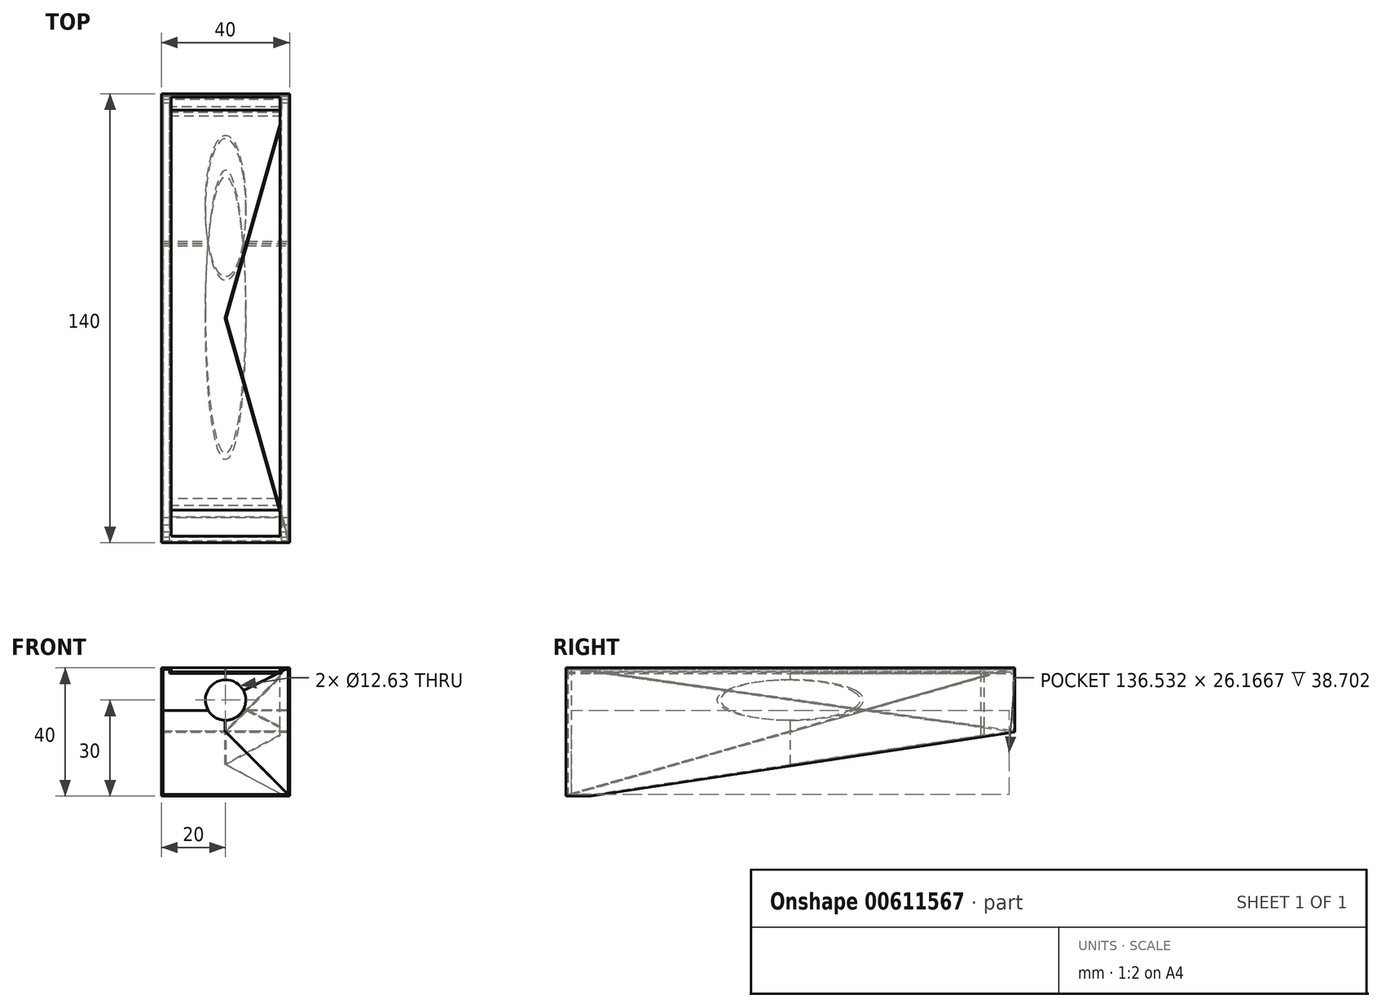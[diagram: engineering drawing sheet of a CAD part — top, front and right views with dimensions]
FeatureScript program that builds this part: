
annotation { "Feature Type Name" : "Feature", "Feature Type Description" : "" }
export const myFeature = defineFeature(function(context is Context, id is Id, definition is map)
    precondition{}
    {
        {
            var Q0;
            Q0=qCreatedBy(makeId("Front.planeOp"),FACE);
            var sketch = newSketch(context, id + "F0", { "sketchPlane" : qUnion([Q0])});
            skLineSegment(sketch, "E0.bottom", {"start": v(-15, 20) * mm, "end": v(15, 20) * mm});
            skLineSegment(sketch, "E0.top", {"start": v(-15, -20) * mm, "end": v(15, -20) * mm});
            skLineSegment(sketch, "E0.left", {"start": v(-20, 15) * mm, "end": v(-20, -15) * mm});
            skLineSegment(sketch, "E0.right", {"start": v(20, 15) * mm, "end": v(20, -15) * mm});
            skPoint(sketch, "E0.middle", {"position": v(0, 0) * mm});
            skPoint(sketch, "E1.visualSharp", {"position": v(-20, -20) * mm});
            skPoint(sketch, "E2.visualSharp", {"position": v(20, -20) * mm});
            skLineSegment(sketch, "E3", {"start": v(-20, -15) * mm, "end": v(20, -15) * mm});
            skLineSegment(sketch, "E4", {"start": v(-20, -15) * mm, "end": v(-20, -11.86) * mm});
            skLineSegment(sketch, "E5", {"start": v(-20, -15) * mm, "end": v(-17, -15) * mm});
            skLineSegment(sketch, "E6", {"start": v(-17, -15) * mm, "end": v(-17, 20) * mm});
            skLineSegment(sketch, "E7", {"start": v(-17, 20) * mm, "end": v(-17, 15) * mm});
            skLineSegment(sketch, "E8", {"start": v(-17, 15) * mm, "end": v(-20, 15) * mm});
            skLineSegment(sketch, "E9.MirrorCS", {"start": v(17, -15) * mm, "end": v(17, 20) * mm});
            skLineSegment(sketch, "E10.MirrorCS", {"start": v(20, 20) * mm, "end": v(20, -15) * mm});
            skLineSegment(sketch, "E11.MirrorCS", {"start": v(17, 15) * mm, "end": v(20, 15) * mm});
            skLineSegment(sketch, "E12", {"start": v(-18.5, 15) * mm, "end": v(-18.5, -15) * mm});
            skLineSegment(sketch, "E13", {"start": v(-18.5, -5.26) * mm, "end": v(-18.5, -3.26) * mm});
            skLineSegment(sketch, "E14", {"start": v(-18.5, 2.74) * mm, "end": v(-18.5, 4.74) * mm});
            skLineSegment(sketch, "E15", {"start": v(-15, -20) * mm, "end": v(-15, -15) * mm});
            skLineSegment(sketch, "E16", {"start": v(-15, -17.5) * mm, "end": v(15, -17.5) * mm});
            skLineSegment(sketch, "E17", {"start": v(15, -17.5) * mm, "end": v(15, -20) * mm});
            skLineSegment(sketch, "E18", {"start": v(15, -17.5) * mm, "end": v(15, -15) * mm});
            skLineSegment(sketch, "E19", {"start": v(-15, -15) * mm, "end": v(-18.54, -18.54) * mm});
            skLineSegment(sketch, "E20", {"start": v(-18.54, -18.54) * mm, "end": v(-16.77, -16.77) * mm});
            skLineSegment(sketch, "E21", {"start": v(-20, -15) * mm, "end": v(-15, -20) * mm});
            skCircle(sketch, "E22", {"center": v(0, -17.5) * mm, "radius": 2.07 * mm});
            skCircle(sketch, "E23", {"center": v(-10.25, -17.5) * mm, "radius": 1.14 * mm});
            skCircle(sketch, "E24", {"center": v(-5.95, -17.5) * mm, "radius": 1.97 * mm});
            skCircle(sketch, "E25.MirrorC", {"center": v(5.95, -17.5) * mm, "radius": 1.97 * mm});
            skCircle(sketch, "E26.MirrorC", {"center": v(10.25, -17.5) * mm, "radius": 1.14 * mm});
            skLineSegment(sketch, "E27", {"start": v(-17, 20) * mm, "end": v(17, 20) * mm});
            skPoint(sketch, "E28.visualSharp", {"position": v(-20, 20) * mm});
            skPoint(sketch, "E29.visualSharp", {"position": v(20, 20) * mm});
            skLineSegment(sketch, "E30", {"start": v(-17, 17.5) * mm, "end": v(17, 17.5) * mm});
            skLineSegment(sketch, "E31", {"start": v(-17, 18.83) * mm, "end": v(17, 18.83) * mm});
            skLineSegment(sketch, "E32", {"start": v(-20, 15) * mm, "end": v(-20, 20) * mm});
            skLineSegment(sketch, "E33", {"start": v(17, 20) * mm, "end": v(20, 20) * mm});
            skLineSegment(sketch, "E34", {"start": v(-20, 20) * mm, "end": v(-17, 20) * mm});
            skLineSegment(sketch, "E35", {"start": v(15, -20) * mm, "end": v(20, -20) * mm});
            skLineSegment(sketch, "E36", {"start": v(20, -15) * mm, "end": v(20, -20) * mm});
            skLineSegment(sketch, "E37", {"start": v(-15, -20) * mm, "end": v(-20, -20) * mm});
            skLineSegment(sketch, "E38", {"start": v(-20, -15) * mm, "end": v(-20, -20) * mm});
            skSolve(sketch);
        }
        {
            var Q0;
            {var subQ5=sQuery(id+"F0.wireOp",EDGE,"E11.MirrorCS");Q0=makeQuery(id+"F0.imprint","IMPRINT",FACE,{"disambiguationData":[TD([[makeQuery(id+"F0.imprint","IMPRINT",EDGE,{"derivedFrom":subQ5}),1.0]])]});}
            var Q1;
            {var subQ0=sQuery(id+"F0.wireOp",EDGE,"E21");var subQ3=sQuery(id+"F0.wireOp",EDGE,"kyP0Ghf2-8tRf-b2os-GJ9Y-R51s7YL5zU5A");var subQ5=makeQuery(id+"F0.imprint","INTERSECT",VERTEX,{"disambiguationData":[OD(0.0)],"derivedFrom":[subQ0,subQ3]});Q1=makeQuery(id+"F0.imprint","IMPRINT",FACE,{"disambiguationData":[TD([[makeQuery(id+"F0.imprint","IMPRINT",EDGE,{"disambiguationData":[TD([[subQ5,-1.0]])],"derivedFrom":subQ3}),-1.0]])]});}
            var Q2;
            {var subQ0=sQuery(id+"F0.wireOp",EDGE,"E21");var subQ3=sQuery(id+"F0.wireOp",EDGE,"kyP0Ghf2-8tRf-b2os-GJ9Y-R51s7YL5zU5A");var subQ5=makeQuery(id+"F0.imprint","INTERSECT",VERTEX,{"disambiguationData":[OD(1.0)],"derivedFrom":[subQ0,subQ3]});Q2=makeQuery(id+"F0.imprint","IMPRINT",FACE,{"disambiguationData":[TD([[makeQuery(id+"F0.imprint","IMPRINT",EDGE,{"disambiguationData":[TD([[subQ5,1.0]])],"derivedFrom":subQ3}),-1.0]])]});}
            var Q3;
            {var subQ1=sQuery(id+"F0.wireOp",EDGE,"E2.filletArc");var subQ3=sQuery(id+"F0.wireOp",EDGE,"8bdb658c-147e-4b0e-9f76-7d081b696ae10.MirrorC");var subQ4=makeQuery(id+"F0.imprint","INTERSECT",VERTEX,{"derivedFrom":[subQ1,subQ3]});Q3=makeQuery(id+"F0.imprint","IMPRINT",FACE,{"disambiguationData":[TD([[makeQuery(id+"F0.imprint","IMPRINT",EDGE,{"disambiguationData":[TD([[subQ4,-1.0]])],"derivedFrom":subQ3}),1.0]])]});}
            var Q4;
            {var subQ1=sQuery(id+"F0.wireOp",EDGE,"E2.filletArc");var subQ3=sQuery(id+"F0.wireOp",EDGE,"8bdb658c-147e-4b0e-9f76-7d081b696ae10.MirrorC");var subQ4=makeQuery(id+"F0.imprint","INTERSECT",VERTEX,{"derivedFrom":[subQ1,subQ3]});Q4=makeQuery(id+"F0.imprint","IMPRINT",FACE,{"disambiguationData":[TD([[makeQuery(id+"F0.imprint","IMPRINT",EDGE,{"disambiguationData":[TD([[subQ4,1.0]])],"derivedFrom":subQ3}),1.0]])]});}
            var Q5;
            {var subQ0=sQuery(id+"F0.wireOp",EDGE,"E7");Q5=makeQuery(id+"F0.imprint","IMPRINT",FACE,{"disambiguationData":[TD([[makeQuery(id+"F0.imprint","IMPRINT",EDGE,{"derivedFrom":subQ0}),-1.0]])]});}
            var Q6;
            {var subQ0=sQuery(id+"F0.wireOp",EDGE,"E8");var subQ1=sQuery(id+"F0.wireOp",EDGE,"E0.left");var subQ2=makeQuery(id+"F0.imprint","INTERSECT",VERTEX,{"derivedFrom":[subQ1,subQ0]});Q6=makeQuery(id+"F0.imprint","IMPRINT",FACE,{"disambiguationData":[TD([[makeQuery(id+"F0.imprint","IMPRINT",EDGE,{"disambiguationData":[TD([[subQ2,-1.0]])],"derivedFrom":subQ1}),1.0]])]});}
            var Q7;
            {var subQ0=sQuery(id+"F0.wireOp",EDGE,"1121410c-8889-4fde-b7d4-53cf977519030.MirrorC");var subQ1=sQuery(id+"F0.wireOp",EDGE,"E0.left");var subQ2=makeQuery(id+"F0.imprint","INTERSECT",VERTEX,{"derivedFrom":[subQ1,subQ0]});Q7=makeQuery(id+"F0.imprint","IMPRINT",FACE,{"disambiguationData":[TD([[makeQuery(id+"F0.imprint","IMPRINT",EDGE,{"disambiguationData":[TD([[subQ2,-1.0]])],"derivedFrom":subQ1}),1.0]])]});}
            var Q8;
            {var subQ1=sQuery(id+"F0.wireOp",EDGE,"E0.left");var subQ5=sQuery(id+"F0.wireOp",EDGE,"3be5d0f7-e66a-4034-bf2c-b5a2b3a159480.MirrorC");var subQ6=makeQuery(id+"F0.imprint","INTERSECT",VERTEX,{"derivedFrom":[subQ1,subQ5]});Q8=makeQuery(id+"F0.imprint","IMPRINT",FACE,{"disambiguationData":[TD([[makeQuery(id+"F0.imprint","IMPRINT",EDGE,{"disambiguationData":[TD([[subQ6,-1.0]])],"derivedFrom":subQ1}),1.0]])]});}
            var Q9;
            {var subQ0=sQuery(id+"F0.wireOp",EDGE,"fb5a3924-ac59-4bed-af84-7003ddc445cf0.MirrorC");var subQ1=sQuery(id+"F0.wireOp",EDGE,"E0.left");var subQ2=makeQuery(id+"F0.imprint","INTERSECT",VERTEX,{"derivedFrom":[subQ1,subQ0]});Q9=makeQuery(id+"F0.imprint","IMPRINT",FACE,{"disambiguationData":[TD([[makeQuery(id+"F0.imprint","IMPRINT",EDGE,{"disambiguationData":[TD([[subQ2,-1.0]])],"derivedFrom":subQ1}),1.0]])]});}
            var Q10;
            {var subQ1=sQuery(id+"F0.wireOp",EDGE,"E0.left");var subQ7=sQuery(id+"F0.wireOp",EDGE,"804b6b5c-8591-4f70-8d60-dec1e7231a500.MirrorC");var subQ9=makeQuery(id+"F0.imprint","INTERSECT",VERTEX,{"derivedFrom":[subQ1,subQ7]});Q10=makeQuery(id+"F0.imprint","IMPRINT",FACE,{"disambiguationData":[TD([[makeQuery(id+"F0.imprint","IMPRINT",EDGE,{"disambiguationData":[TD([[subQ9,-1.0]])],"derivedFrom":subQ1}),1.0]])]});}
            var Q11;
            {var subQ0=sQuery(id+"F0.wireOp",EDGE,"UupdKjqE-uhdA-a4V7-ZC8J-dwgjoSrKTdi6");var subQ1=sQuery(id+"F0.wireOp",EDGE,"E0.left");var subQ2=makeQuery(id+"F0.imprint","INTERSECT",VERTEX,{"derivedFrom":[subQ1,subQ0]});Q11=makeQuery(id+"F0.imprint","IMPRINT",FACE,{"disambiguationData":[TD([[makeQuery(id+"F0.imprint","IMPRINT",EDGE,{"disambiguationData":[TD([[subQ2,-1.0]])],"derivedFrom":subQ1}),1.0]])]});}
            var Q12;
            {var subQ1=sQuery(id+"F0.wireOp",EDGE,"E5");var subQ3=sQuery(id+"F0.wireOp",EDGE,"kyP0Ghf2-8tRf-b2os-GJ9Y-R51s7YL5zU5A");var subQ4=makeQuery(id+"F0.imprint","INTERSECT",VERTEX,{"derivedFrom":[subQ1,subQ3]});Q12=makeQuery(id+"F0.imprint","IMPRINT",FACE,{"disambiguationData":[TD([[makeQuery(id+"F0.imprint","IMPRINT",EDGE,{"disambiguationData":[TD([[subQ4,-1.0]])],"derivedFrom":subQ3}),-1.0]])]});}
            var Q13;
            {var subQ0=sQuery(id+"F0.wireOp",EDGE,"819de83c-ce93-4df8-b3f5-d03e4e11402c4.MirrorC");var subQ1=sQuery(id+"F0.wireOp",EDGE,"E9.MirrorCS");var subQ2=makeQuery(id+"F0.imprint","INTERSECT",VERTEX,{"derivedFrom":[subQ1,subQ0]});Q13=makeQuery(id+"F0.imprint","IMPRINT",FACE,{"disambiguationData":[TD([[makeQuery(id+"F0.imprint","IMPRINT",EDGE,{"disambiguationData":[TD([[subQ2,-1.0]])],"derivedFrom":subQ1}),-1.0]])]});}
            var Q14;
            {var subQ0=sQuery(id+"F0.wireOp",EDGE,"819de83c-ce93-4df8-b3f5-d03e4e11402c3.MirrorC");var subQ1=sQuery(id+"F0.wireOp",EDGE,"E9.MirrorCS");var subQ2=makeQuery(id+"F0.imprint","INTERSECT",VERTEX,{"derivedFrom":[subQ1,subQ0]});Q14=makeQuery(id+"F0.imprint","IMPRINT",FACE,{"disambiguationData":[TD([[makeQuery(id+"F0.imprint","IMPRINT",EDGE,{"disambiguationData":[TD([[subQ2,-1.0]])],"derivedFrom":subQ1}),-1.0]])]});}
            var Q15;
            {var subQ0=sQuery(id+"F0.wireOp",EDGE,"819de83c-ce93-4df8-b3f5-d03e4e11402c7.MirrorC");var subQ1=sQuery(id+"F0.wireOp",EDGE,"E9.MirrorCS");var subQ2=makeQuery(id+"F0.imprint","INTERSECT",VERTEX,{"derivedFrom":[subQ1,subQ0]});Q15=makeQuery(id+"F0.imprint","IMPRINT",FACE,{"disambiguationData":[TD([[makeQuery(id+"F0.imprint","IMPRINT",EDGE,{"disambiguationData":[TD([[subQ2,-1.0]])],"derivedFrom":subQ1}),-1.0]])]});}
            var Q16;
            {var subQ0=sQuery(id+"F0.wireOp",EDGE,"819de83c-ce93-4df8-b3f5-d03e4e11402c8.MirrorC");var subQ1=sQuery(id+"F0.wireOp",EDGE,"E9.MirrorCS");var subQ2=makeQuery(id+"F0.imprint","INTERSECT",VERTEX,{"derivedFrom":[subQ1,subQ0]});Q16=makeQuery(id+"F0.imprint","IMPRINT",FACE,{"disambiguationData":[TD([[makeQuery(id+"F0.imprint","IMPRINT",EDGE,{"disambiguationData":[TD([[subQ2,-1.0]])],"derivedFrom":subQ1}),-1.0]])]});}
            var Q17;
            {var subQ0=sQuery(id+"F0.wireOp",EDGE,"819de83c-ce93-4df8-b3f5-d03e4e11402c5.MirrorC");var subQ1=sQuery(id+"F0.wireOp",EDGE,"E9.MirrorCS");var subQ2=makeQuery(id+"F0.imprint","INTERSECT",VERTEX,{"derivedFrom":[subQ1,subQ0]});Q17=makeQuery(id+"F0.imprint","IMPRINT",FACE,{"disambiguationData":[TD([[makeQuery(id+"F0.imprint","IMPRINT",EDGE,{"disambiguationData":[TD([[subQ2,-1.0]])],"derivedFrom":subQ1}),-1.0]])]});}
            var Q18;
            {var subQ0=sQuery(id+"F0.wireOp",EDGE,"E11.MirrorCS");Q18=makeQuery(id+"F0.imprint","IMPRINT",FACE,{"disambiguationData":[TD([[makeQuery(id+"F0.imprint","IMPRINT",EDGE,{"derivedFrom":subQ0}),-1.0]])]});}
            var Q19;
            {var subQ1=sQuery(id+"F0.wireOp",EDGE,"E15");var subQ3=sQuery(id+"F0.wireOp",EDGE,"kyP0Ghf2-8tRf-b2os-GJ9Y-R51s7YL5zU5A");var subQ4=makeQuery(id+"F0.imprint","INTERSECT",VERTEX,{"derivedFrom":[subQ1,subQ3]});Q19=makeQuery(id+"F0.imprint","IMPRINT",FACE,{"disambiguationData":[TD([[makeQuery(id+"F0.imprint","IMPRINT",EDGE,{"disambiguationData":[TD([[subQ4,1.0]])],"derivedFrom":subQ3}),-1.0]])]});}
            var Q20;
            {var subQ1=sQuery(id+"F0.wireOp",EDGE,"E4");Q20=makeQuery(id+"F0.imprint","IMPRINT",FACE,{"disambiguationData":[TD([[makeQuery(id+"F0.imprint","IMPRINT",EDGE,{"derivedFrom":subQ1}),-1.0]])]});}
            var Q21;
            {var subQ3=sQuery(id+"F0.wireOp",EDGE,"E9.MirrorCS");var subQ5=sQuery(id+"F0.wireOp",EDGE,"8bdb658c-147e-4b0e-9f76-7d081b696ae10.MirrorC");var subQ8=makeQuery(id+"F0.imprint","INTERSECT",VERTEX,{"derivedFrom":[subQ3,subQ5]});Q21=makeQuery(id+"F0.imprint","IMPRINT",FACE,{"disambiguationData":[TD([[makeQuery(id+"F0.imprint","IMPRINT",EDGE,{"disambiguationData":[TD([[subQ8,-1.0]])],"derivedFrom":subQ3}),-1.0]])]});}
            var Q22;
            {var subQ1=sQuery(id+"F0.wireOp",EDGE,"E0.top");Q22=makeQuery(id+"F0.imprint","IMPRINT",FACE,{"disambiguationData":[TD([[makeQuery(id+"F0.imprint","IMPRINT",EDGE,{"derivedFrom":subQ1}),1.0]])]});}
            var Q23;
            {var subQ0=sQuery(id+"F0.wireOp",EDGE,"E18");Q23=makeQuery(id+"F0.imprint","IMPRINT",FACE,{"disambiguationData":[TD([[makeQuery(id+"F0.imprint","IMPRINT",EDGE,{"derivedFrom":subQ0}),-1.0]])]});}
            var Q24;
            {var subQ0=sQuery(id+"F0.wireOp",EDGE,"E8");var subQ5=sQuery(id+"F0.wireOp",EDGE,"E12");var subQ7=makeQuery(id+"F0.imprint","INTERSECT",VERTEX,{"derivedFrom":[subQ0,subQ5]});Q24=makeQuery(id+"F0.imprint","IMPRINT",FACE,{"disambiguationData":[TD([[makeQuery(id+"F0.imprint","IMPRINT",EDGE,{"disambiguationData":[TD([[subQ7,-1.0]])],"derivedFrom":subQ5}),1.0]])]});}
            var Q25;
            {var subQ0=sQuery(id+"F0.wireOp",EDGE,"3be5d0f7-e66a-4034-bf2c-b5a2b3a159480.MirrorC");var subQ1=sQuery(id+"F0.wireOp",EDGE,"E6");var subQ2=makeQuery(id+"F0.imprint","INTERSECT",VERTEX,{"derivedFrom":[subQ1,subQ0]});Q25=makeQuery(id+"F0.imprint","IMPRINT",FACE,{"disambiguationData":[TD([[makeQuery(id+"F0.imprint","IMPRINT",EDGE,{"disambiguationData":[TD([[subQ2,-1.0]])],"derivedFrom":subQ1}),1.0]])]});}
            var Q26;
            {var subQ3=sQuery(id+"F0.wireOp",EDGE,"fb5a3924-ac59-4bed-af84-7003ddc445cf0.MirrorC");var subQ7=sQuery(id+"F0.wireOp",EDGE,"E6");var subQ9=makeQuery(id+"F0.imprint","INTERSECT",VERTEX,{"derivedFrom":[subQ7,subQ3]});Q26=makeQuery(id+"F0.imprint","IMPRINT",FACE,{"disambiguationData":[TD([[makeQuery(id+"F0.imprint","IMPRINT",EDGE,{"disambiguationData":[TD([[subQ9,-1.0]])],"derivedFrom":subQ7}),1.0]])]});}
            var Q27;
            {var subQ0=sQuery(id+"F0.wireOp",EDGE,"804b6b5c-8591-4f70-8d60-dec1e7231a500.MirrorC");var subQ1=sQuery(id+"F0.wireOp",EDGE,"E6");var subQ2=makeQuery(id+"F0.imprint","INTERSECT",VERTEX,{"derivedFrom":[subQ1,subQ0]});Q27=makeQuery(id+"F0.imprint","IMPRINT",FACE,{"disambiguationData":[TD([[makeQuery(id+"F0.imprint","IMPRINT",EDGE,{"disambiguationData":[TD([[subQ2,-1.0]])],"derivedFrom":subQ1}),1.0]])]});}
            var Q28;
            {var subQ3=sQuery(id+"F0.wireOp",EDGE,"UupdKjqE-uhdA-a4V7-ZC8J-dwgjoSrKTdi6");var subQ5=sQuery(id+"F0.wireOp",EDGE,"E6");var subQ6=makeQuery(id+"F0.imprint","INTERSECT",VERTEX,{"derivedFrom":[subQ5,subQ3]});Q28=makeQuery(id+"F0.imprint","IMPRINT",FACE,{"disambiguationData":[TD([[makeQuery(id+"F0.imprint","IMPRINT",EDGE,{"disambiguationData":[TD([[subQ6,-1.0]])],"derivedFrom":subQ5}),1.0]])]});}
            var Q29;
            {var subQ0=sQuery(id+"F0.wireOp",EDGE,"kyP0Ghf2-8tRf-b2os-GJ9Y-R51s7YL5zU5A");var subQ5=sQuery(id+"F0.wireOp",EDGE,"E16");var subQ6=makeQuery(id+"F0.imprint","INTERSECT",VERTEX,{"derivedFrom":[subQ5,subQ0]});Q29=makeQuery(id+"F0.imprint","IMPRINT",FACE,{"disambiguationData":[TD([[makeQuery(id+"F0.imprint","IMPRINT",EDGE,{"disambiguationData":[TD([[subQ6,-1.0]])],"derivedFrom":subQ5}),1.0]])]});}
            var Q30;
            {var subQ1=sQuery(id+"F0.wireOp",EDGE,"E19");Q30=makeQuery(id+"F0.imprint","IMPRINT",FACE,{"disambiguationData":[TD([[makeQuery(id+"F0.imprint","IMPRINT",EDGE,{"derivedFrom":subQ1}),1.0]])]});}
            var Q31;
            {var subQ1=sQuery(id+"F0.wireOp",EDGE,"E1.filletArc");var subQ3=sQuery(id+"F0.wireOp",EDGE,"E20");var subQ4=makeQuery(id+"F0.imprint","INTERSECT",VERTEX,{"derivedFrom":[subQ1,subQ3]});Q31=makeQuery(id+"F0.imprint","IMPRINT",FACE,{"disambiguationData":[TD([[makeQuery(id+"F0.imprint","IMPRINT",EDGE,{"disambiguationData":[TD([[subQ4,-1.0]])],"derivedFrom":subQ3}),-1.0]])]});}
            var Q32;
            {var subQ1=sQuery(id+"F0.wireOp",EDGE,"E1.filletArc");var subQ3=sQuery(id+"F0.wireOp",EDGE,"E20");var subQ4=makeQuery(id+"F0.imprint","INTERSECT",VERTEX,{"derivedFrom":[subQ1,subQ3]});Q32=makeQuery(id+"F0.imprint","IMPRINT",FACE,{"disambiguationData":[TD([[makeQuery(id+"F0.imprint","IMPRINT",EDGE,{"disambiguationData":[TD([[subQ4,-1.0]])],"derivedFrom":subQ3}),-1.0]])]});}
            var Q33;
            {var subQ0=sQuery(id+"F0.wireOp",EDGE,"E19");Q33=makeQuery(id+"F0.imprint","IMPRINT",FACE,{"disambiguationData":[TD([[makeQuery(id+"F0.imprint","IMPRINT",EDGE,{"derivedFrom":subQ0}),-1.0]])]});}
            var Q34;
            {var subQ1=sQuery(id+"F0.wireOp",EDGE,"E1.filletArc");var subQ3=sQuery(id+"F0.wireOp",EDGE,"E20");var subQ4=makeQuery(id+"F0.imprint","INTERSECT",VERTEX,{"derivedFrom":[subQ1,subQ3]});Q34=makeQuery(id+"F0.imprint","IMPRINT",FACE,{"disambiguationData":[TD([[makeQuery(id+"F0.imprint","IMPRINT",EDGE,{"disambiguationData":[TD([[subQ4,-1.0]])],"derivedFrom":subQ3}),1.0]])]});}
            var Q35;
            {var subQ1=sQuery(id+"F0.wireOp",EDGE,"E31");var subQ14=sQuery(id+"F0.wireOp",EDGE,"E7");var subQ15=makeQuery(id+"F0.imprint","INTERSECT",VERTEX,{"derivedFrom":[subQ14,subQ1]});Q35=makeQuery(id+"F0.imprint","IMPRINT",FACE,{"disambiguationData":[TD([[makeQuery(id+"F0.imprint","IMPRINT",EDGE,{"disambiguationData":[TD([[subQ15,1.0]])],"derivedFrom":subQ14}),1.0]])]});}
            var Q36;
            {var subQ8=sQuery(id+"F0.wireOp",EDGE,"E30");Q36=makeQuery(id+"F0.imprint","IMPRINT",FACE,{"disambiguationData":[TD([[makeQuery(id+"F0.imprint","IMPRINT",EDGE,{"derivedFrom":subQ8}),1.0]])]});}
            var Q37;
            {var subQ3=sQuery(id+"F0.wireOp",EDGE,"E37");Q37=makeQuery(id+"F0.imprint","IMPRINT",FACE,{"disambiguationData":[TD([[makeQuery(id+"F0.imprint","IMPRINT",EDGE,{"derivedFrom":subQ3}),-1.0]])]});}
            var Q38;
            {var subQ0=sQuery(id+"F0.wireOp",EDGE,"E6");Q38=makeQuery(id+"F0.imprint","IMPRINT",FACE,{"disambiguationData":[TD([[makeQuery(id+"F0.imprint","IMPRINT",EDGE,{"derivedFrom":subQ0}),-1.0]])]});}
            var Q39;
            {var subQ0=sQuery(id+"F0.wireOp",EDGE,"E25.MirrorC");var subQ1=sQuery(id+"F0.wireOp",EDGE,"E16");var subQ2=makeQuery(id+"F0.imprint","INTERSECT",VERTEX,{"disambiguationData":[OD(0.0)],"derivedFrom":[subQ1,subQ0]});Q39=makeQuery(id+"F0.imprint","IMPRINT",FACE,{"disambiguationData":[TD([[makeQuery(id+"F0.imprint","IMPRINT",EDGE,{"disambiguationData":[TD([[subQ2,-1.0]])],"derivedFrom":subQ1}),1.0]])]});}
            var Q40;
            {var subQ0=sQuery(id+"F0.wireOp",EDGE,"E25.MirrorC");var subQ1=sQuery(id+"F0.wireOp",EDGE,"E16");var subQ2=makeQuery(id+"F0.imprint","INTERSECT",VERTEX,{"disambiguationData":[OD(0.0)],"derivedFrom":[subQ1,subQ0]});Q40=makeQuery(id+"F0.imprint","IMPRINT",FACE,{"disambiguationData":[TD([[makeQuery(id+"F0.imprint","IMPRINT",EDGE,{"disambiguationData":[TD([[subQ2,-1.0]])],"derivedFrom":subQ1}),-1.0]])]});}
            var Q41;
            {var subQ0=sQuery(id+"F0.wireOp",EDGE,"E26.MirrorC");var subQ1=sQuery(id+"F0.wireOp",EDGE,"E16");var subQ2=makeQuery(id+"F0.imprint","INTERSECT",VERTEX,{"disambiguationData":[OD(0.0)],"derivedFrom":[subQ1,subQ0]});Q41=makeQuery(id+"F0.imprint","IMPRINT",FACE,{"disambiguationData":[TD([[makeQuery(id+"F0.imprint","IMPRINT",EDGE,{"disambiguationData":[TD([[subQ2,-1.0]])],"derivedFrom":subQ1}),-1.0]])]});}
            var Q42;
            {var subQ0=sQuery(id+"F0.wireOp",EDGE,"E26.MirrorC");var subQ1=sQuery(id+"F0.wireOp",EDGE,"E16");var subQ2=makeQuery(id+"F0.imprint","INTERSECT",VERTEX,{"disambiguationData":[OD(0.0)],"derivedFrom":[subQ1,subQ0]});Q42=makeQuery(id+"F0.imprint","IMPRINT",FACE,{"disambiguationData":[TD([[makeQuery(id+"F0.imprint","IMPRINT",EDGE,{"disambiguationData":[TD([[subQ2,-1.0]])],"derivedFrom":subQ1}),1.0]])]});}
            var Q43;
            {var subQ0=sQuery(id+"F0.wireOp",EDGE,"E22");var subQ1=sQuery(id+"F0.wireOp",EDGE,"E16");var subQ2=makeQuery(id+"F0.imprint","INTERSECT",VERTEX,{"disambiguationData":[OD(0.0)],"derivedFrom":[subQ1,subQ0]});Q43=makeQuery(id+"F0.imprint","IMPRINT",FACE,{"disambiguationData":[TD([[makeQuery(id+"F0.imprint","IMPRINT",EDGE,{"disambiguationData":[TD([[subQ2,-1.0]])],"derivedFrom":subQ1}),1.0]])]});}
            var Q44;
            {var subQ0=sQuery(id+"F0.wireOp",EDGE,"E22");var subQ1=sQuery(id+"F0.wireOp",EDGE,"E16");var subQ2=makeQuery(id+"F0.imprint","INTERSECT",VERTEX,{"disambiguationData":[OD(0.0)],"derivedFrom":[subQ1,subQ0]});Q44=makeQuery(id+"F0.imprint","IMPRINT",FACE,{"disambiguationData":[TD([[makeQuery(id+"F0.imprint","IMPRINT",EDGE,{"disambiguationData":[TD([[subQ2,-1.0]])],"derivedFrom":subQ1}),-1.0]])]});}
            var Q45;
            {var subQ0=sQuery(id+"F0.wireOp",EDGE,"E24");var subQ1=sQuery(id+"F0.wireOp",EDGE,"E16");var subQ2=makeQuery(id+"F0.imprint","INTERSECT",VERTEX,{"disambiguationData":[OD(0.0)],"derivedFrom":[subQ1,subQ0]});Q45=makeQuery(id+"F0.imprint","IMPRINT",FACE,{"disambiguationData":[TD([[makeQuery(id+"F0.imprint","IMPRINT",EDGE,{"disambiguationData":[TD([[subQ2,-1.0]])],"derivedFrom":subQ1}),-1.0]])]});}
            var Q46;
            {var subQ0=sQuery(id+"F0.wireOp",EDGE,"E23");var subQ1=sQuery(id+"F0.wireOp",EDGE,"E16");var subQ2=makeQuery(id+"F0.imprint","INTERSECT",VERTEX,{"disambiguationData":[OD(0.0)],"derivedFrom":[subQ1,subQ0]});Q46=makeQuery(id+"F0.imprint","IMPRINT",FACE,{"disambiguationData":[TD([[makeQuery(id+"F0.imprint","IMPRINT",EDGE,{"disambiguationData":[TD([[subQ2,-1.0]])],"derivedFrom":subQ1}),1.0]])]});}
            extrude(context, id + "F1", {"entities" : qUnion([Q0, Q1, Q2, Q3, Q4, Q5, Q6, Q7, Q8, Q9, Q10, Q11, Q12, Q13, Q14, Q15, Q16, Q17, Q18, Q19, Q20, Q21, Q22, Q23, Q24, Q25, Q26, Q27, Q28, Q29, Q30, Q31, Q32, Q33, Q34, Q35, Q36, Q37, Q38, Q39, Q40, Q41, Q42, Q43, Q44, Q45, Q46]), "depth" : 140 * mm, "offsetDistance" : 25 * mm});
        }
        {
            var Q0;
            Q0=makeQuery(id+"F1.opExtrude","SWEPT_FACE",FACE,{"disambiguationData":[OSD([sQuery(id+"F0.wireOp",EDGE,"E10.MirrorCS"),sQuery(id+"F0.wireOp",EDGE,"E36")])]});
            var sketch = newSketch(context, id + "F2", { "sketchPlane" : qUnion([Q0])});
            skLineSegment(sketch, "E39", {"start": v(-132.04, -20) * mm, "end": v(0, 0) * mm});
            skLineSegment(sketch, "E40", {"start": v(-132.04, -20) * mm, "end": v(-133.12, -12.86) * mm});
            skLineSegment(sketch, "E41", {"start": v(-133.12, -12.86) * mm, "end": v(0, 7.3) * mm});
            skLineSegment(sketch, "E42", {"start": v(-133.12, -12.86) * mm, "end": v(-140, -13.9) * mm});
            skLineSegment(sketch, "E43", {"start": v(-132.04, -20) * mm, "end": v(-143.14, -21.68) * mm});
            skLineSegment(sketch, "E44", {"start": v(-143.14, -21.68) * mm, "end": v(-144.32, -13.9) * mm});
            skLineSegment(sketch, "E45", {"start": v(-140, -13.9) * mm, "end": v(-144.22, -14.54) * mm});
            skLineSegment(sketch, "E46", {"start": v(0, 20) * mm, "end": v(0, 0) * mm});
            skLineSegment(sketch, "E47", {"start": v(-140, 20) * mm, "end": v(-140, -20) * mm});
            skLineSegment(sketch, "E48", {"start": v(-140, -20) * mm, "end": v(-132.04, -20) * mm});
            skSolve(sketch);
        }
        {
            var Q0;
            {var subQ0=sQuery(id+"F2.wireOp",EDGE,"E39");Q0=makeQuery(id+"F2.imprint","IMPRINT",FACE,{"disambiguationData":[TD([[makeQuery(id+"F2.imprint","IMPRINT",EDGE,{"derivedFrom":subQ0}),-1.0]])]});}
            extrude(context, id + "F3", {"entities" : qUnion([Q0]), "operationType" : NewBodyOperationType.REMOVE, "oppositeDirection" : true, "depth" : 50 * mm, "offsetDistance" : 25 * mm});
        }
        {
            var Q0;
            {var subQ0=sQuery(id+"F2.wireOp",EDGE,"E39");Q0=makeQuery(id+"F2.imprint","IMPRINT",FACE,{"disambiguationData":[TD([[makeQuery(id+"F2.imprint","IMPRINT",EDGE,{"derivedFrom":subQ0}),1.0]])]});}
            var Q1;
            {var subQ0=sQuery(id+"F2.wireOp",EDGE,"E40");Q1=makeQuery(id+"F2.imprint","IMPRINT",FACE,{"disambiguationData":[TD([[makeQuery(id+"F2.imprint","IMPRINT",EDGE,{"derivedFrom":subQ0}),1.0]])]});}
            extrude(context, id + "F4", {"entities" : qUnion([Q0, Q1]), "operationType" : NewBodyOperationType.ADD, "oppositeDirection" : true, "depth" : 40 * mm, "offsetDistance" : 25 * mm});
        }
        {
            var Q0;
            Q0=makeQuery(id+"F4.boolean.opBoolean","MERGE",FACE,{"derivedFrom":[makeQuery(id+"F1.opExtrude","CAP_FACE",FACE,{"disambiguationData":[OSD([sQuery(id+"F0.wireOp",EDGE,"E0.top"),sQuery(id+"F0.wireOp",EDGE,"E0.left"),sQuery(id+"F0.wireOp",EDGE,"E4"),sQuery(id+"F0.wireOp",EDGE,"E10.MirrorCS"),sQuery(id+"F0.wireOp",EDGE,"E16"),sQuery(id+"F0.wireOp",EDGE,"E23"),sQuery(id+"F0.wireOp",EDGE,"E24"),sQuery(id+"F0.wireOp",EDGE,"E27"),sQuery(id+"F0.wireOp",EDGE,"E32"),sQuery(id+"F0.wireOp",EDGE,"E33"),sQuery(id+"F0.wireOp",EDGE,"E34"),sQuery(id+"F0.wireOp",EDGE,"E35"),sQuery(id+"F0.wireOp",EDGE,"E36"),sQuery(id+"F0.wireOp",EDGE,"E37"),sQuery(id+"F0.wireOp",EDGE,"E38")])],"isStart":false}),makeQuery(id+"F4.opExtrude","SWEPT_FACE",FACE,{"disambiguationData":[OSD([sQuery(id+"F2.wireOp",EDGE,"E47")])]})]});
            var Q1;
            Q1=makeQuery(id+"F1.opExtrude","SWEPT_BODY",BODY,{"disambiguationData":[OSD([sQuery(id+"F0.wireOp",EDGE,"E0.top"),sQuery(id+"F0.wireOp",EDGE,"E0.left"),sQuery(id+"F0.wireOp",EDGE,"E4"),sQuery(id+"F0.wireOp",EDGE,"E10.MirrorCS"),sQuery(id+"F0.wireOp",EDGE,"E16"),sQuery(id+"F0.wireOp",EDGE,"E23"),sQuery(id+"F0.wireOp",EDGE,"E24"),sQuery(id+"F0.wireOp",EDGE,"E27"),sQuery(id+"F0.wireOp",EDGE,"E32"),sQuery(id+"F0.wireOp",EDGE,"E33"),sQuery(id+"F0.wireOp",EDGE,"E34"),sQuery(id+"F0.wireOp",EDGE,"E35"),sQuery(id+"F0.wireOp",EDGE,"E36"),sQuery(id+"F0.wireOp",EDGE,"E37"),sQuery(id+"F0.wireOp",EDGE,"E38")])]});
            shell(context, id + "F5", {"entities" : qUnion([Q0]), "parts" : qUnion([Q1]), "thickness" : 0.5 * mm});
        }
        {
            var Q0;
            Q0=makeQuery(id+"F1.opExtrude","SWEPT_FACE",FACE,{"disambiguationData":[OSD([sQuery(id+"F0.wireOp",EDGE,"E27"),sQuery(id+"F0.wireOp",EDGE,"E33"),sQuery(id+"F0.wireOp",EDGE,"E34")])]});
            var sketch = newSketch(context, id + "F6", { "sketchPlane" : qUnion([Q0])});
            skLineSegment(sketch, "E49", {"start": v(-20, 0) * mm, "end": v(19.7, -140) * mm});
            skLineSegment(sketch, "E50", {"start": v(19.7, -140) * mm, "end": v(20, -140) * mm});
            skLineSegment(sketch, "E51", {"start": v(20, -140) * mm, "end": v(-19.7, 0) * mm});
            skLineSegment(sketch, "E52.MirrorCS", {"start": v(20, 0) * mm, "end": v(-19.7, -140) * mm});
            skLineSegment(sketch, "E53.MirrorCS", {"start": v(-20, -140) * mm, "end": v(19.7, 0) * mm});
            skLineSegment(sketch, "E54", {"start": v(-0.15, -70) * mm, "end": v(0.15, -70) * mm});
            skLineSegment(sketch, "E55", {"start": v(0.15, -70) * mm, "end": v(0, -70) * mm});
            skLineSegment(sketch, "E56", {"start": v(0, -70) * mm, "end": v(0, -70.1) * mm});
            skSolve(sketch);
        }
        {
            var Q0;
            Q0=qSketchRegion(id+"F6",true);
            var Q1;
            {var subQ1=sQuery(id+"F6.wireOp",EDGE,"E49");var subQ3=sQuery(id+"F6.wireOp",EDGE,"E52.MirrorCS");var subQ4=makeQuery(id+"F6.imprint","INTERSECT",VERTEX,{"derivedFrom":[subQ1,subQ3]});Q1=makeQuery(id+"F6.imprint","IMPRINT",FACE,{"disambiguationData":[TD([[makeQuery(id+"F6.imprint","IMPRINT",EDGE,{"disambiguationData":[TD([[subQ4,1.0]])],"derivedFrom":subQ1}),-1.0]])]});}
            var Q2;
            {var subQ1=sQuery(id+"F6.wireOp",EDGE,"E51");var subQ3=sQuery(id+"F6.wireOp",EDGE,"E53.MirrorCS");var subQ4=makeQuery(id+"F6.imprint","INTERSECT",VERTEX,{"derivedFrom":[subQ1,subQ3]});Q2=makeQuery(id+"F6.imprint","IMPRINT",FACE,{"disambiguationData":[TD([[makeQuery(id+"F6.imprint","IMPRINT",EDGE,{"disambiguationData":[TD([[subQ4,1.0]])],"derivedFrom":subQ1}),-1.0]])]});}
            var Q3;
            {var subQ4=sQuery(id+"F6.wireOp",EDGE,"E53.MirrorCS");var subQ6=sQuery(id+"F6.wireOp",EDGE,"E51");var subQ8=makeQuery(id+"F6.imprint","INTERSECT",VERTEX,{"derivedFrom":[subQ6,subQ4]});Q3=makeQuery(id+"F6.imprint","IMPRINT",FACE,{"disambiguationData":[TD([[makeQuery(id+"F6.imprint","IMPRINT",EDGE,{"disambiguationData":[TD([[subQ8,1.0]])],"derivedFrom":subQ4}),1.0]])]});}
            var Q4;
            {var subQ0=sQuery(id+"F2.wireOp",EDGE,"E39");Q4=makeQuery(id+"F4.boolean.opBoolean","MERGE",FACE,{"derivedFrom":[makeQuery(id+"F3.boolean.opBoolean","COPY",FACE,{"derivedFrom":makeQuery(id+"F3.opExtrude","SWEPT_FACE",FACE,{"disambiguationData":[OSD([subQ0])]})}),makeQuery(id+"F4.opExtrude","SWEPT_FACE",FACE,{"disambiguationData":[OSD([subQ0])]})]});}
            extrude(context, id + "F7", {"entities" : qUnion([Q0, Q1, Q2, Q3]), "operationType" : NewBodyOperationType.ADD, "endBound" : BoundingType.UP_TO_SURFACE, "oppositeDirection" : true, "depth" : 25 * mm, "endBoundEntityFace" : qUnion([Q4]), "offsetDistance" : 25 * mm});
        }
        {
            var Q0;
            Q0=makeQuery(id+"F1.opExtrude","SWEPT_FACE",FACE,{"disambiguationData":[OSD([sQuery(id+"F0.wireOp",EDGE,"E10.MirrorCS"),sQuery(id+"F0.wireOp",EDGE,"E36")])]});
            var sketch = newSketch(context, id + "F8", { "sketchPlane" : qUnion([Q0])});
            skLineSegment(sketch, "E57", {"start": v(-140, -20) * mm, "end": v(0, 20) * mm});
            skLineSegment(sketch, "E58", {"start": v(0, 20) * mm, "end": v(-1.06, 20) * mm});
            skLineSegment(sketch, "E59", {"start": v(-1.06, 20) * mm, "end": v(-140, -19.7) * mm});
            skLineSegment(sketch, "E60", {"start": v(-140, 20) * mm, "end": v(0, 0) * mm});
            skLineSegment(sketch, "E61", {"start": v(0, 0.3) * mm, "end": v(-137.95, 20) * mm});
            skSolve(sketch);
        }
        {
            var Q0;
            Q0=qSketchRegion(id+"F8",true);
            var Q1;
            {var subQ0=sQuery(id+"F8.wireOp",EDGE,"E61");var subQ1=sQuery(id+"F8.wireOp",EDGE,"E59");var subQ2=makeQuery(id+"F8.imprint","INTERSECT",VERTEX,{"derivedFrom":[subQ1,subQ0]});Q1=makeQuery(id+"F8.imprint","IMPRINT",FACE,{"disambiguationData":[TD([[makeQuery(id+"F8.imprint","IMPRINT",EDGE,{"disambiguationData":[TD([[subQ2,-1.0]])],"derivedFrom":subQ1}),-1.0]])]});}
            var Q2;
            {var subQ0=sQuery(id+"F8.wireOp",EDGE,"E60");var subQ1=sQuery(id+"F8.wireOp",EDGE,"E57");var subQ2=makeQuery(id+"F8.imprint","INTERSECT",VERTEX,{"derivedFrom":[subQ1,subQ0]});Q2=makeQuery(id+"F8.imprint","IMPRINT",FACE,{"disambiguationData":[TD([[makeQuery(id+"F8.imprint","IMPRINT",EDGE,{"disambiguationData":[TD([[subQ2,-1.0]])],"derivedFrom":subQ1}),-1.0]])]});}
            var Q3;
            {var subQ0=sQuery(id+"F8.wireOp",EDGE,"E57");var subQ4=sQuery(id+"F8.wireOp",EDGE,"E60");var subQ5=makeQuery(id+"F8.imprint","INTERSECT",VERTEX,{"derivedFrom":[subQ0,subQ4]});Q3=makeQuery(id+"F8.imprint","IMPRINT",FACE,{"disambiguationData":[TD([[makeQuery(id+"F8.imprint","IMPRINT",EDGE,{"disambiguationData":[TD([[subQ5,1.0]])],"derivedFrom":subQ4}),-1.0]])]});}
            var Q4;
            Q4=makeQuery(id+"F1.opExtrude","SWEPT_FACE",FACE,{"disambiguationData":[OSD([sQuery(id+"F0.wireOp",EDGE,"E0.left"),sQuery(id+"F0.wireOp",EDGE,"E4"),sQuery(id+"F0.wireOp",EDGE,"E32"),sQuery(id+"F0.wireOp",EDGE,"E38")])]});
            extrude(context, id + "F9", {"entities" : qUnion([Q0, Q1, Q2, Q3]), "operationType" : NewBodyOperationType.ADD, "endBound" : BoundingType.UP_TO_SURFACE, "oppositeDirection" : true, "depth" : 25 * mm, "endBoundEntityFace" : qUnion([Q4]), "offsetDistance" : 25 * mm});
        }
        {
            var Q0;
            Q0=makeQuery(id+"F1.opExtrude","SWEPT_FACE",FACE,{"disambiguationData":[OSD([sQuery(id+"F0.wireOp",EDGE,"E0.left"),sQuery(id+"F0.wireOp",EDGE,"E4"),sQuery(id+"F0.wireOp",EDGE,"E32"),sQuery(id+"F0.wireOp",EDGE,"E38")])]});
            var sketch = newSketch(context, id + "F10", { "sketchPlane" : qUnion([Q0])});
            skLineSegment(sketch, "E62", {"start": v(132.04, -20) * mm, "end": v(140, -20) * mm});
            skLineSegment(sketch, "E63", {"start": v(140, -20) * mm, "end": v(141.57, -20) * mm});
            skLineSegment(sketch, "E64", {"start": v(141.57, -20) * mm, "end": v(142.03, -23.42) * mm});
            skLineSegment(sketch, "E65", {"start": v(142.03, -23.42) * mm, "end": v(132.04, -21.88) * mm});
            skLineSegment(sketch, "E66", {"start": v(132.04, -21.88) * mm, "end": v(132.04, -20) * mm});
            skSolve(sketch);
        }
        {
            var Q0;
            Q0=qSketchRegion(id+"F10",true);
            extrude(context, id + "F11", {"entities" : qUnion([Q0]), "operationType" : NewBodyOperationType.REMOVE, "oppositeDirection" : true, "depth" : 1000 * mm, "offsetDistance" : 25 * mm});
        }
        {
            var Q0;
            Q0=makeQuery(id+"F1.opExtrude","CAP_FACE",FACE,{"disambiguationData":[OSD([sQuery(id+"F0.wireOp",EDGE,"E0.top"),sQuery(id+"F0.wireOp",EDGE,"E0.left"),sQuery(id+"F0.wireOp",EDGE,"E4"),sQuery(id+"F0.wireOp",EDGE,"E10.MirrorCS"),sQuery(id+"F0.wireOp",EDGE,"E16"),sQuery(id+"F0.wireOp",EDGE,"E23"),sQuery(id+"F0.wireOp",EDGE,"E24"),sQuery(id+"F0.wireOp",EDGE,"E27"),sQuery(id+"F0.wireOp",EDGE,"E32"),sQuery(id+"F0.wireOp",EDGE,"E33"),sQuery(id+"F0.wireOp",EDGE,"E34"),sQuery(id+"F0.wireOp",EDGE,"E35"),sQuery(id+"F0.wireOp",EDGE,"E36"),sQuery(id+"F0.wireOp",EDGE,"E37"),sQuery(id+"F0.wireOp",EDGE,"E38")])],"isStart":true});
            var sketch = newSketch(context, id + "F12", { "sketchPlane" : qUnion([Q0])});
            skCircle(sketch, "E67", {"center": v(0, 10) * mm, "radius": 6.32 * mm});
            skPoint(sketch, "E67.centerSnap0", {"position": v(20, 10) * mm});
            skSolve(sketch);
        }
        {
            var Q0;
            Q0=qSketchRegion(id+"F12",true);
            var Q1;
            {var subQ0=sQuery(id+"F0.wireOp",EDGE,"E34");var subQ1=sQuery(id+"F0.wireOp",EDGE,"E33");var subQ2=sQuery(id+"F0.wireOp",EDGE,"E27");var subQ3=makeQuery(id+"F1.opExtrude","CAP_EDGE",EDGE,{"disambiguationData":[OSD([subQ2,subQ1,subQ0])],"isStart":false});var subQ4=sQuery(id+"F0.wireOp",EDGE,"E32");Q1=makeQuery(id+"F7.boolean.opBoolean","MERGE",FACE,{"derivedFrom":[makeQuery(id+"F4.boolean.opBoolean","MERGE",FACE,{"derivedFrom":[makeQuery(id+"F1.opExtrude","CAP_FACE",FACE,{"disambiguationData":[OSD([sQuery(id+"F0.wireOp",EDGE,"E0.top"),sQuery(id+"F0.wireOp",EDGE,"E0.left"),sQuery(id+"F0.wireOp",EDGE,"E4"),sQuery(id+"F0.wireOp",EDGE,"E10.MirrorCS"),sQuery(id+"F0.wireOp",EDGE,"E16"),sQuery(id+"F0.wireOp",EDGE,"E23"),sQuery(id+"F0.wireOp",EDGE,"E24"),subQ2,subQ4,subQ1,subQ0,sQuery(id+"F0.wireOp",EDGE,"E35"),sQuery(id+"F0.wireOp",EDGE,"E36"),sQuery(id+"F0.wireOp",EDGE,"E37"),sQuery(id+"F0.wireOp",EDGE,"E38")])],"isStart":false}),makeQuery(id+"F4.opExtrude","SWEPT_FACE",FACE,{"disambiguationData":[OSD([sQuery(id+"F2.wireOp",EDGE,"E47")])]})]}),makeQuery(id+"F7.opExtrude","SWEPT_FACE",FACE,{"disambiguationData":[OSD([sQuery(id+"F6.wireOp",EDGE,"E50")])]}),makeQuery(id+"F7.opExtrude","SWEPT_FACE",FACE,{"disambiguationData":[OSD([subQ2,subQ1,subQ0]),TDD([makeQuery(id+"F6.imprint","IMPRINT",EDGE,{"disambiguationData":[TD([[makeQuery(id+"F6.imprint","INTERSECT",VERTEX,{"derivedFrom":[subQ3,sQuery(id+"F6.wireOp",EDGE,"E52.MirrorCS")]}),1.0]])],"derivedFrom":subQ3})])]})]});}
            extrude(context, id + "F13", {"entities" : qUnion([Q0]), "operationType" : NewBodyOperationType.REMOVE, "endBound" : BoundingType.UP_TO_SURFACE, "oppositeDirection" : true, "depth" : 25 * mm, "endBoundEntityFace" : qUnion([Q1]), "offsetDistance" : 25 * mm});
        }
    });
